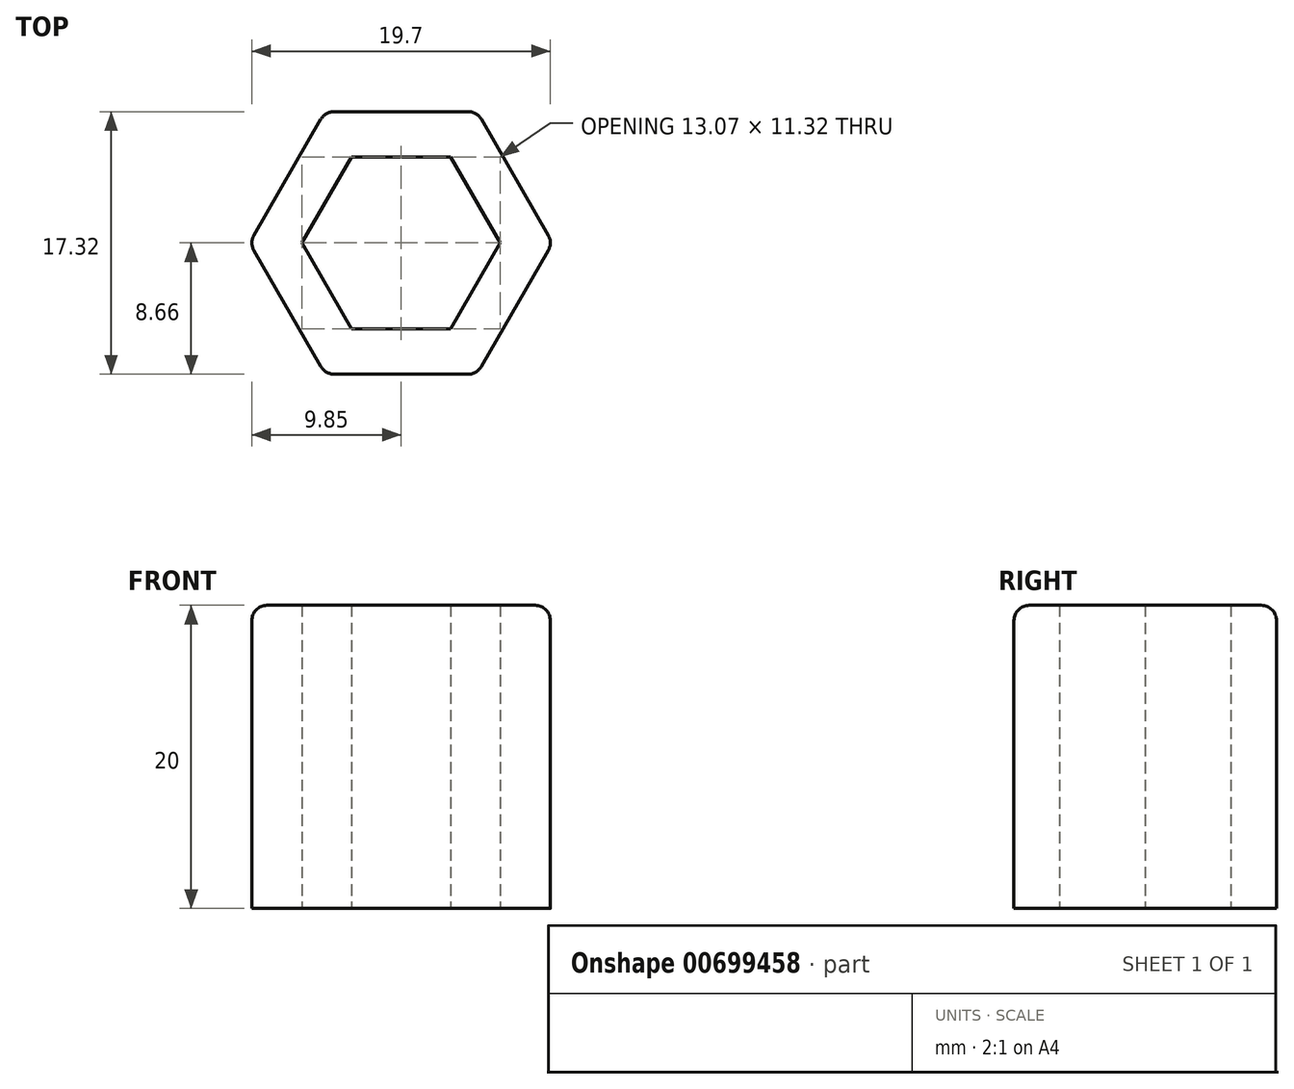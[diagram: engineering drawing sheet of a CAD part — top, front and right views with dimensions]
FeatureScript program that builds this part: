
annotation { "Feature Type Name" : "Feature", "Feature Type Description" : "" }
export const myFeature = defineFeature(function(context is Context, id is Id, definition is map)
    precondition{}
    {
        {
            var Q0;
            Q0=qCreatedBy(makeId("Top.planeOp"),FACE);
            var sketch = newSketch(context, id + "F0", { "sketchPlane" : qUnion([Q0])});
            skLineSegment(sketch, "E0.bottom", {"start": v(10, 10) * mm, "end": v(-10, 10) * mm, "construction": true});
            skLineSegment(sketch, "E0.top", {"start": v(10, -10) * mm, "end": v(-10, -10) * mm, "construction": true});
            skLineSegment(sketch, "E0.left", {"start": v(10, 10) * mm, "end": v(10, -10) * mm, "construction": true});
            skLineSegment(sketch, "E0.right", {"start": v(-10, 10) * mm, "end": v(-10, -10) * mm, "construction": true});
            skPoint(sketch, "E0.middle", {"position": v(0, 0) * mm});
            skCircle(sketch, "E1.cCircle", {"center": v(0, 0) * mm, "radius": 8.66 * mm, "construction": true});
            skLineSegment(sketch, "E1.0", {"start": v(5, 8.66) * mm, "end": v(10, 0) * mm});
            skLineSegment(sketch, "E1.1", {"start": v(10, 0) * mm, "end": v(5, -8.66) * mm});
            skLineSegment(sketch, "E1.2", {"start": v(5, -8.66) * mm, "end": v(-5, -8.66) * mm});
            skLineSegment(sketch, "E1.3", {"start": v(-5, -8.66) * mm, "end": v(-10, 0) * mm});
            skLineSegment(sketch, "E1.4", {"start": v(-10, 0) * mm, "end": v(-5, 8.66) * mm});
            skLineSegment(sketch, "E1.5", {"start": v(-5, 8.66) * mm, "end": v(5, 8.66) * mm});
            skPoint(sketch, "E1.0.midPoint", {"position": v(7.5, 4.33) * mm});
            skLineSegment(sketch, "E2.0", {"start": v(-3.27, -5.66) * mm, "end": v(-6.54, 0) * mm});
            skLineSegment(sketch, "E2.1", {"start": v(-3.27, 5.66) * mm, "end": v(3.27, 5.66) * mm});
            skLineSegment(sketch, "E2.2", {"start": v(3.27, 5.66) * mm, "end": v(6.54, 0) * mm});
            skLineSegment(sketch, "E2.3", {"start": v(-6.54, 0) * mm, "end": v(-3.27, 5.66) * mm});
            skLineSegment(sketch, "E2.4", {"start": v(6.54, 0) * mm, "end": v(3.27, -5.66) * mm});
            skLineSegment(sketch, "E2.5", {"start": v(3.27, -5.66) * mm, "end": v(-3.27, -5.66) * mm});
            skSolve(sketch);
        }
        {
            var Q0;
            Q0=qSketchRegion(id+"F0",true);
            extrude(context, id + "F1", {"entities" : qUnion([Q0]), "depth" : 20 * mm, "offsetDistance" : 25 * mm});
        }
        {
            var Q0;
            Q0=makeQuery(id+"F1.opExtrude","CAP_EDGE",EDGE,{"disambiguationData":[OSD([sQuery(id+"F0.wireOp",EDGE,"E1.3")])],"isStart":false});
            var Q1;
            Q1=makeQuery(id+"F1.opExtrude","CAP_EDGE",EDGE,{"disambiguationData":[OSD([sQuery(id+"F0.wireOp",EDGE,"E1.4")])],"isStart":false});
            var Q2;
            Q2=makeQuery(id+"F1.opExtrude","CAP_EDGE",EDGE,{"disambiguationData":[OSD([sQuery(id+"F0.wireOp",EDGE,"E1.5")])],"isStart":false});
            var Q3;
            Q3=makeQuery(id+"F1.opExtrude","CAP_EDGE",EDGE,{"disambiguationData":[OSD([sQuery(id+"F0.wireOp",EDGE,"E1.0")])],"isStart":false});
            var Q4;
            Q4=makeQuery(id+"F1.opExtrude","CAP_EDGE",EDGE,{"disambiguationData":[OSD([sQuery(id+"F0.wireOp",EDGE,"E1.1")])],"isStart":false});
            var Q5;
            Q5=makeQuery(id+"F1.opExtrude","CAP_EDGE",EDGE,{"disambiguationData":[OSD([sQuery(id+"F0.wireOp",EDGE,"E1.2")])],"isStart":false});
            var Q6;
            Q6=makeQuery(id+"F1.opExtrude","SWEPT_EDGE",EDGE,{"disambiguationData":[OSD([sQuery(id+"F0.wireOp",EDGE,"E1.2"),sQuery(id+"F0.wireOp",EDGE,"E1.3")])]});
            var Q7;
            Q7=makeQuery(id+"F1.opExtrude","SWEPT_EDGE",EDGE,{"disambiguationData":[OSD([sQuery(id+"F0.wireOp",EDGE,"E1.0"),sQuery(id+"F0.wireOp",EDGE,"E1.1")])]});
            var Q8;
            Q8=makeQuery(id+"F1.opExtrude","SWEPT_EDGE",EDGE,{"disambiguationData":[OSD([sQuery(id+"F0.wireOp",EDGE,"E1.1"),sQuery(id+"F0.wireOp",EDGE,"E1.2")])]});
            var Q9;
            Q9=makeQuery(id+"F1.opExtrude","SWEPT_EDGE",EDGE,{"disambiguationData":[OSD([sQuery(id+"F0.wireOp",EDGE,"E1.0"),sQuery(id+"F0.wireOp",EDGE,"E1.5")])]});
            var Q10;
            Q10=makeQuery(id+"F1.opExtrude","SWEPT_EDGE",EDGE,{"disambiguationData":[OSD([sQuery(id+"F0.wireOp",EDGE,"E1.4"),sQuery(id+"F0.wireOp",EDGE,"E1.5")])]});
            var Q11;
            Q11=makeQuery(id+"F1.opExtrude","SWEPT_EDGE",EDGE,{"disambiguationData":[OSD([sQuery(id+"F0.wireOp",EDGE,"E1.3"),sQuery(id+"F0.wireOp",EDGE,"E1.4")])]});
            fillet(context, id + "F2", {"entities" : qUnion([Q0, Q1, Q2, Q3, Q4, Q5, Q6, Q7, Q8, Q9, Q10, Q11]), "radius" : 1 * mm, "tangentPropagation" : true, "allowEdgeOverflow" : false});
        }
    });
